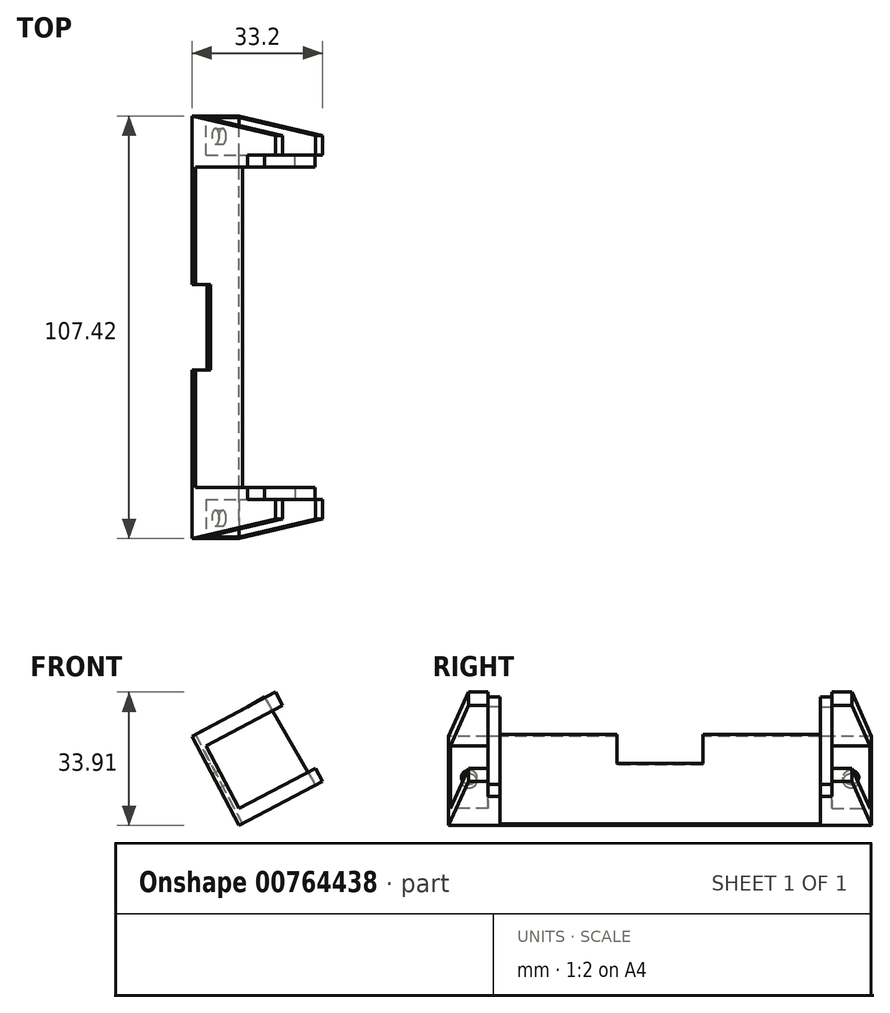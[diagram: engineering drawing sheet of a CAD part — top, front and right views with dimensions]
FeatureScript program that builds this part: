
annotation { "Feature Type Name" : "Feature", "Feature Type Description" : "" }
export const myFeature = defineFeature(function(context is Context, id is Id, definition is map)
    precondition{}
    {
        {
            var Q0;
            Q0=qCreatedBy(makeId("Right.planeOp"),FACE);
            var sketch = newSketch(context, id + "F0", { "sketchPlane" : qUnion([Q0])});
            skLineSegment(sketch, "E0.left", {"start": v(-41.6, -6.42) * mm, "end": v(-41.6, 6.2) * mm});
            skPoint(sketch, "E1.visualSharp", {"position": v(-41.6, 10.2) * mm});
            skPoint(sketch, "E2.visualSharp", {"position": v(-41.6, -10.42) * mm});
            skPoint(sketch, "E3.visualSharp", {"position": v(41.56, 10.2) * mm});
            skPoint(sketch, "E4.visualSharp", {"position": v(41.56, -10.42) * mm});
            skPoint(sketch, "E5.visualSharp", {"position": v(-38.3, -8.6) * mm});
            skPoint(sketch, "E6.visualSharp", {"position": v(38.25, -8.6) * mm});
            skLineSegment(sketch, "E7.bottom", {"start": v(-37.14, 9.3) * mm, "end": v(37.1, 9.3) * mm});
            skLineSegment(sketch, "E7.top", {"start": v(-37.14, -9.52) * mm, "end": v(37.1, -9.52) * mm});
            skLineSegment(sketch, "E7.left", {"start": v(-40.14, 6.3) * mm, "end": v(-40.14, -6.52) * mm});
            skLineSegment(sketch, "E7.right", {"start": v(40.1, 6.3) * mm, "end": v(40.1, -6.52) * mm});
            skArc(sketch, "E8.filletArc", {"start": v(-37.14, 9.3) * mm, "mid": v(-39.26, 8.42) * mm, "end": v(-40.14, 6.3) * mm});
            skPoint(sketch, "E9.visualSharp", {"position": v(-40.14, -9.52) * mm});
            skArc(sketch, "E9.filletArc", {"start": v(-40.14, -6.52) * mm, "mid": v(-39.26, -8.64) * mm, "end": v(-37.14, -9.52) * mm});
            skArc(sketch, "E10.filletArc", {"start": v(37.1, -9.52) * mm, "mid": v(39.21, -8.64) * mm, "end": v(40.1, -6.52) * mm});
            skArc(sketch, "E11.filletArc", {"start": v(40.1, 6.3) * mm, "mid": v(39.21, 8.42) * mm, "end": v(37.1, 9.3) * mm});
            skLineSegment(sketch, "E12.bottom", {"start": v(-43.7, 11.11) * mm, "end": v(43.7, 11.11) * mm});
            skLineSegment(sketch, "E12.top", {"start": v(-43.7, -11.11) * mm, "end": v(43.7, -11.11) * mm});
            skLineSegment(sketch, "E12.left", {"start": v(-43.7, 11.11) * mm, "end": v(-43.7, -11.11) * mm});
            skLineSegment(sketch, "E12.right", {"start": v(43.7, 11.11) * mm, "end": v(43.7, -11.11) * mm});
            skPoint(sketch, "E12.middle", {"position": v(0, 0) * mm});
            skLineSegment(sketch, "E13.bottom", {"start": v(-43.7, 11.11) * mm, "end": v(-41.6, 11.11) * mm});
            skLineSegment(sketch, "E13.top", {"start": v(-43.7, -11.11) * mm, "end": v(-41.6, -11.11) * mm});
            skLineSegment(sketch, "E13.right", {"start": v(-41.6, 11.11) * mm, "end": v(-41.6, -11.11) * mm});
            skLineSegment(sketch, "E14.bottom", {"start": v(43.7, 11.11) * mm, "end": v(41.56, 11.11) * mm});
            skLineSegment(sketch, "E14.top", {"start": v(43.7, -11.11) * mm, "end": v(41.56, -11.11) * mm});
            skLineSegment(sketch, "E14.right", {"start": v(41.56, 11.11) * mm, "end": v(41.56, -11.11) * mm});
            skSolve(sketch);
        }
        {
            var Q0;
            Q0=qSketchRegion(id+"F0",true);
            extrude(context, id + "F1", {"entities" : qUnion([Q0]), "depth" : 3 * mm, "offsetDistance" : 25 * mm});
        }
        {
            var Q0;
            Q0=makeQuery(id+"F1.opExtrude","SWEPT_FACE",FACE,{"disambiguationData":[OSD([sQuery(id+"F0.wireOp",EDGE,"E12.left")])]});
            var sketch = newSketch(context, id + "F2", { "sketchPlane" : qUnion([Q0])});
            skLineSegment(sketch, "E15", {"start": v(0, 11.11) * mm, "end": v(-12.83, 11.11) * mm});
            skLineSegment(sketch, "E16", {"start": v(-12.83, 11.11) * mm, "end": v(0, -11.11) * mm});
            skSolve(sketch);
        }
        {
            var Q0;
            Q0=qSketchRegion(id+"F2",true);
            var Q1;
            Q1=makeQuery(id+"F2.imprint","IMPRINT",FACE,{"disambiguationData":[TD([[makeQuery(id+"F2.imprint","IMPRINT",EDGE,{"derivedFrom":sQuery(id+"F2.wireOp",EDGE,"E15")}),1.0]])]});
            extrude(context, id + "F3", {"entities" : qUnion([Q0, Q1]), "operationType" : NewBodyOperationType.ADD, "oppositeDirection" : true, "depth" : 3 * mm, "offsetDistance" : 25 * mm});
        }
        {
            var Q0;
            Q0=makeQuery(id+"F1.opExtrude","SWEPT_FACE",FACE,{"disambiguationData":[OSD([sQuery(id+"F0.wireOp",EDGE,"E12.right")])]});
            var sketch = newSketch(context, id + "F4", { "sketchPlane" : qUnion([Q0])});
            skLineSegment(sketch, "E17", {"start": v(0, 11.11) * mm, "end": v(0, -11.11) * mm});
            skLineSegment(sketch, "E18", {"start": v(0, -11.11) * mm, "end": v(12.82, 11.12) * mm});
            skLineSegment(sketch, "E19", {"start": v(12.82, 11.12) * mm, "end": v(0, 11.11) * mm});
            skSolve(sketch);
        }
        {
            var Q0;
            Q0=makeQuery(id+"F4.imprint","IMPRINT",FACE,{"disambiguationData":[TD([[makeQuery(id+"F4.imprint","IMPRINT",EDGE,{"derivedFrom":sQuery(id+"F4.wireOp",EDGE,"E17")}),1.0]])]});
            extrude(context, id + "F5", {"entities" : qUnion([Q0]), "operationType" : NewBodyOperationType.ADD, "oppositeDirection" : true, "depth" : 3 * mm, "offsetDistance" : 25 * mm});
        }
        {
            var Q0;
            Q0=makeQuery(id+"F3.opExtrude","SWEPT_FACE",FACE,{"disambiguationData":[OSD([sQuery(id+"F2.wireOp",EDGE,"E16")])]});
            extrude(context, id + "F6", {"entities" : qUnion([Q0]), "operationType" : NewBodyOperationType.ADD, "depth" : 5 * mm, "offsetDistance" : 25 * mm});
        }
        {
            var Q0;
            {var subQ0=sQuery(id+"F2.wireOp",EDGE,"E16");var subQ1=sQuery(id+"F0.wireOp",EDGE,"E12.left");Q0=makeQuery(id+"F6.boolean.opBoolean","MERGE",FACE,{"derivedFrom":[makeQuery(id+"F3.boolean.opBoolean","MERGE",FACE,{"derivedFrom":[makeQuery(id+"F1.opExtrude","SWEPT_FACE",FACE,{"disambiguationData":[OSD([subQ1])]}),makeQuery(id+"F3.opExtrude","CAP_FACE",FACE,{"disambiguationData":[OSD([subQ1,sQuery(id+"F2.wireOp",EDGE,"E15"),subQ0])],"isStart":true})]}),makeQuery(id+"F6.opExtrude","SWEPT_FACE",FACE,{"disambiguationData":[OSD([subQ0]),TDD([makeQuery(id+"F3.opExtrude","CAP_EDGE",EDGE,{"disambiguationData":[OSD([subQ0])],"isStart":true})])]})]});}
            var sketch = newSketch(context, id + "F7", { "sketchPlane" : qUnion([Q0])});
            skLineSegment(sketch, "E20", {"start": v(-2.17, -12.36) * mm, "end": v(-5.2, -14.11) * mm});
            skLineSegment(sketch, "E21", {"start": v(-5.2, -14.11) * mm, "end": v(-17.16, 8.61) * mm});
            skSolve(sketch);
        }
        {
            var Q0;
            {var subQ3=sQuery(id+"F7.wireOp",EDGE,"E21");Q0=makeQuery(id+"F7.imprint","IMPRINT",FACE,{"disambiguationData":[TD([[makeQuery(id+"F7.imprint","IMPRINT",EDGE,{"derivedFrom":subQ3}),-1.0]])]});}
            extrude(context, id + "F8", {"entities" : qUnion([Q0]), "operationType" : NewBodyOperationType.ADD, "oppositeDirection" : true, "depth" : 3 * mm, "offsetDistance" : 25 * mm});
        }
        {
            var Q0;
            Q0=makeQuery(id+"F5.opExtrude","SWEPT_FACE",FACE,{"disambiguationData":[OSD([sQuery(id+"F4.wireOp",EDGE,"E18")])]});
            extrude(context, id + "F9", {"entities" : qUnion([Q0]), "operationType" : NewBodyOperationType.ADD, "depth" : 5 * mm, "offsetDistance" : 25 * mm});
        }
        {
            var Q0;
            {var subQ0=sQuery(id+"F4.wireOp",EDGE,"E18");Q0=makeQuery(id+"F9.boolean.opBoolean","MERGE",FACE,{"derivedFrom":[makeQuery(id+"F5.boolean.opBoolean","MERGE",FACE,{"derivedFrom":[makeQuery(id+"F1.opExtrude","SWEPT_FACE",FACE,{"disambiguationData":[OSD([sQuery(id+"F0.wireOp",EDGE,"E12.right")])]}),makeQuery(id+"F5.opExtrude","CAP_FACE",FACE,{"disambiguationData":[OSD([sQuery(id+"F4.wireOp",EDGE,"E17"),subQ0,sQuery(id+"F4.wireOp",EDGE,"E19")])],"isStart":true})]}),makeQuery(id+"F9.opExtrude","SWEPT_FACE",FACE,{"disambiguationData":[OSD([subQ0]),TDD([makeQuery(id+"F5.opExtrude","CAP_EDGE",EDGE,{"disambiguationData":[OSD([subQ0])],"isStart":true})])]})]});}
            var sketch = newSketch(context, id + "F10", { "sketchPlane" : qUnion([Q0])});
            skLineSegment(sketch, "E22", {"start": v(4.33, -13.61) * mm, "end": v(5.2, -14.11) * mm});
            skLineSegment(sketch, "E23", {"start": v(5.2, -14.11) * mm, "end": v(17.16, 8.62) * mm});
            skSolve(sketch);
        }
        {
            var Q0;
            Q0=makeQuery(id+"F10.imprint","IMPRINT",FACE,{"disambiguationData":[TD([[makeQuery(id+"F10.imprint","IMPRINT",EDGE,{"derivedFrom":sQuery(id+"F10.wireOp",EDGE,"E22")}),1.0]])]});
            extrude(context, id + "F11", {"entities" : qUnion([Q0]), "operationType" : NewBodyOperationType.ADD, "oppositeDirection" : true, "depth" : 3 * mm, "offsetDistance" : 25 * mm});
        }
        {
            var Q0;
            Q0=makeQuery(id+"F11.opExtrude","SWEPT_FACE",FACE,{"disambiguationData":[OSD([sQuery(id+"F10.wireOp",EDGE,"E23")])]});
            extrude(context, id + "F12", {"entities" : qUnion([Q0]), "operationType" : NewBodyOperationType.ADD, "depth" : 16 * mm, "offsetDistance" : 25 * mm});
        }
        {
            var Q0;
            Q0=makeQuery(id+"F8.opExtrude","SWEPT_FACE",FACE,{"disambiguationData":[OSD([sQuery(id+"F7.wireOp",EDGE,"E21")])]});
            extrude(context, id + "F13", {"entities" : qUnion([Q0]), "operationType" : NewBodyOperationType.ADD, "depth" : 16 * mm, "offsetDistance" : 25 * mm});
        }
        {
            var Q0;
            Q0=makeQuery(id+"F13.opExtrude","SWEPT_FACE",FACE,{"disambiguationData":[OSD([sQuery(id+"F7.wireOp",EDGE,"E20"),sQuery(id+"F7.wireOp",EDGE,"E21")])]});
            var sketch = newSketch(context, id + "F14", { "sketchPlane" : qUnion([Q0])});
            skLineSegment(sketch, "E24", {"start": v(-27.17, 43.7) * mm, "end": v(-27.17, -43.7) * mm});
            skLineSegment(sketch, "E25", {"start": v(-27.17, -43.7) * mm, "end": v(-26.17, -43.7) * mm});
            skLineSegment(sketch, "E26", {"start": v(-26.17, -43.7) * mm, "end": v(-26.17, 43.7) * mm});
            skLineSegment(sketch, "E27", {"start": v(-26.17, 43.7) * mm, "end": v(-27.17, 43.7) * mm});
            skSolve(sketch);
        }
        {
            var Q0;
            {var subQ0=sQuery(id+"F14.wireOp",EDGE,"E27");Q0=makeQuery(id+"F14.imprint","IMPRINT",FACE,{"disambiguationData":[TD([[makeQuery(id+"F14.imprint","IMPRINT",EDGE,{"derivedFrom":subQ0}),-1.0]])]});}
            var Q1;
            {var subQ5=sQuery(id+"F14.wireOp",EDGE,"E25");Q1=makeQuery(id+"F14.imprint","IMPRINT",FACE,{"disambiguationData":[TD([[makeQuery(id+"F14.imprint","IMPRINT",EDGE,{"derivedFrom":subQ5}),1.0]])]});}
            extrude(context, id + "F15", {"entities" : qUnion([Q0, Q1]), "oppositeDirection" : true, "depth" : 25.68 * mm, "offsetDistance" : 25 * mm});
        }
        {
            var Q0;
            Q0=makeQuery(id+"F15.opExtrude","SWEPT_FACE",FACE,{"disambiguationData":[OSD([sQuery(id+"F14.wireOp",EDGE,"E25")])]});
            extrude(context, id + "F16", {"entities" : qUnion([Q0]), "depth" : 10 * mm, "offsetDistance" : 25 * mm});
        }
        {
            var Q0;
            Q0=makeQuery(id+"F16.opExtrude","SWEPT_FACE",FACE,{"disambiguationData":[OSD([sQuery(id+"F14.wireOp",EDGE,"E25"),sQuery(id+"F14.wireOp",EDGE,"E26")])]});
            extrude(context, id + "F17", {"entities" : qUnion([Q0]), "depth" : 2 * mm, "offsetDistance" : 25 * mm});
        }
        {
            var Q0;
            Q0=makeQuery(id+"F15.opExtrude","SWEPT_FACE",FACE,{"disambiguationData":[OSD([sQuery(id+"F14.wireOp",EDGE,"E27")])]});
            extrude(context, id + "F18", {"entities" : qUnion([Q0]), "depth" : 10 * mm, "offsetDistance" : 25 * mm});
        }
        {
            var Q0;
            Q0=makeQuery(id+"F18.opExtrude","SWEPT_FACE",FACE,{"disambiguationData":[OSD([sQuery(id+"F7.wireOp",EDGE,"E20"),sQuery(id+"F7.wireOp",EDGE,"E21"),sQuery(id+"F14.wireOp",EDGE,"E26"),sQuery(id+"F14.wireOp",EDGE,"E27")])]});
            extrude(context, id + "F19", {"entities" : qUnion([Q0]), "depth" : 2 * mm, "offsetDistance" : 25 * mm});
        }
        {
            var Q0;
            Q0=makeQuery(id+"F15.opExtrude","SWEPT_BODY",BODY,{"disambiguationData":[OSD([sQuery(id+"F14.wireOp",EDGE,"E24"),sQuery(id+"F14.wireOp",EDGE,"E25"),sQuery(id+"F14.wireOp",EDGE,"E26"),sQuery(id+"F14.wireOp",EDGE,"E27")])]});
            var Q1;
            Q1=makeQuery(id+"F17.opExtrude","SWEPT_BODY",BODY,{"disambiguationData":[OSD([sQuery(id+"F14.wireOp",EDGE,"E25"),sQuery(id+"F14.wireOp",EDGE,"E26")])]});
            var Q2;
            Q2=makeQuery(id+"F16.opExtrude","SWEPT_BODY",BODY,{"disambiguationData":[OSD([sQuery(id+"F14.wireOp",EDGE,"E25")])]});
            var Q3;
            Q3=makeQuery(id+"F19.opExtrude","SWEPT_BODY",BODY,{"disambiguationData":[OSD([sQuery(id+"F7.wireOp",EDGE,"E20"),sQuery(id+"F7.wireOp",EDGE,"E21"),sQuery(id+"F14.wireOp",EDGE,"E26"),sQuery(id+"F14.wireOp",EDGE,"E27")])]});
            var Q4;
            Q4=makeQuery(id+"F18.opExtrude","SWEPT_BODY",BODY,{"disambiguationData":[OSD([sQuery(id+"F14.wireOp",EDGE,"E27")])]});
            booleanBodies(context, id + "F20", {"operationType" : BooleanOperationType.UNION, "tools" : qUnion([Q0, Q1, Q2, Q3, Q4])});
        }
        {
            var Q0;
            Q0=makeQuery(id+"F15.opExtrude","SWEPT_BODY",BODY,{"disambiguationData":[OSD([sQuery(id+"F14.wireOp",EDGE,"E24"),sQuery(id+"F14.wireOp",EDGE,"E25"),sQuery(id+"F14.wireOp",EDGE,"E26"),sQuery(id+"F14.wireOp",EDGE,"E27")])]});
            var Q1;
            Q1=makeQuery(id+"F1.opExtrude","SWEPT_BODY",BODY,{"disambiguationData":[OSD([sQuery(id+"F0.wireOp",EDGE,"E7.bottom"),sQuery(id+"F0.wireOp",EDGE,"E7.top"),sQuery(id+"F0.wireOp",EDGE,"E7.left"),sQuery(id+"F0.wireOp",EDGE,"E7.right"),sQuery(id+"F0.wireOp",EDGE,"E8.filletArc"),sQuery(id+"F0.wireOp",EDGE,"E9.filletArc"),sQuery(id+"F0.wireOp",EDGE,"E10.filletArc"),sQuery(id+"F0.wireOp",EDGE,"E11.filletArc"),sQuery(id+"F0.wireOp",EDGE,"E12.bottom"),sQuery(id+"F0.wireOp",EDGE,"E12.top"),sQuery(id+"F0.wireOp",EDGE,"E13.bottom"),sQuery(id+"F0.wireOp",EDGE,"E13.top"),sQuery(id+"F0.wireOp",EDGE,"E12.left"),sQuery(id+"F0.wireOp",EDGE,"E14.bottom"),sQuery(id+"F0.wireOp",EDGE,"E14.top"),sQuery(id+"F0.wireOp",EDGE,"E12.right")])]});
            booleanBodies(context, id + "F21", {"operationType" : BooleanOperationType.UNION, "tools" : qUnion([Q0, Q1])});
        }
        {
            var Q0;
            Q0=makeQuery(id+"F19.opExtrude","CAP_FACE",FACE,{"disambiguationData":[OSD([sQuery(id+"F7.wireOp",EDGE,"E20"),sQuery(id+"F7.wireOp",EDGE,"E21"),sQuery(id+"F14.wireOp",EDGE,"E26"),sQuery(id+"F14.wireOp",EDGE,"E27")])],"isStart":false});
            extrude(context, id + "F22", {"entities" : qUnion([Q0]), "operationType" : NewBodyOperationType.ADD, "depth" : 21 * mm, "offsetDistance" : 25 * mm});
        }
        {
            var Q0;
            {var subQ0=sQuery(id+"F14.wireOp",EDGE,"E27");var subQ1=sQuery(id+"F14.wireOp",EDGE,"E26");var subQ2=sQuery(id+"F7.wireOp",EDGE,"E21");var subQ3=sQuery(id+"F7.wireOp",EDGE,"E20");var subQ4=makeQuery(id+"F18.opExtrude","SWEPT_EDGE",EDGE,{"disambiguationData":[OSD([subQ3,subQ2,subQ1,subQ0]),TDD([makeQuery(id+"F15.opExtrude","CAP_VERTEX",VERTEX,{"disambiguationData":[OSD([subQ3,subQ2,subQ1,subQ0])],"isStart":true})])]});var subQ5=sQuery(id+"F14.wireOp",EDGE,"E25");Q0=makeQuery(id+"F22.boolean.opBoolean","MERGE",FACE,{"derivedFrom":[makeQuery(id+"F21.opBoolean","MERGE",FACE,{"derivedFrom":[makeQuery(id+"F13.opExtrude","SWEPT_FACE",FACE,{"disambiguationData":[OSD([subQ3,subQ2])]}),makeQuery(id+"F20.opBoolean","MERGE",FACE,{"derivedFrom":[makeQuery(id+"F15.opExtrude","CAP_FACE",FACE,{"disambiguationData":[OSD([sQuery(id+"F14.wireOp",EDGE,"E24"),subQ5,subQ1,subQ0])],"isStart":true}),makeQuery(id+"F16.opExtrude","SWEPT_FACE",FACE,{"disambiguationData":[OSD([subQ5]),TDD([makeQuery(id+"F15.opExtrude","CAP_EDGE",EDGE,{"disambiguationData":[OSD([subQ5])],"isStart":true})])]}),makeQuery(id+"F17.opExtrude","SWEPT_FACE",FACE,{"disambiguationData":[OSD([subQ5,subQ1]),TDD([makeQuery(id+"F16.opExtrude","SWEPT_EDGE",EDGE,{"disambiguationData":[OSD([subQ5,subQ1]),TDD([makeQuery(id+"F15.opExtrude","CAP_VERTEX",VERTEX,{"disambiguationData":[OSD([subQ5,subQ1])],"isStart":true})])]})])]}),makeQuery(id+"F18.opExtrude","SWEPT_FACE",FACE,{"disambiguationData":[OSD([subQ0]),TDD([makeQuery(id+"F15.opExtrude","CAP_EDGE",EDGE,{"disambiguationData":[OSD([subQ0])],"isStart":true})])]}),makeQuery(id+"F19.opExtrude","SWEPT_FACE",FACE,{"disambiguationData":[OSD([subQ3,subQ2,subQ1,subQ0]),TDD([subQ4])]})]})]}),makeQuery(id+"F22.opExtrude","SWEPT_FACE",FACE,{"disambiguationData":[OSD([subQ3,subQ2,subQ1,subQ0]),TDD([makeQuery(id+"F19.opExtrude","CAP_EDGE",EDGE,{"disambiguationData":[OSD([subQ3,subQ2,subQ1,subQ0]),TDD([subQ4])],"isStart":false})])]})]});}
            var sketch = newSketch(context, id + "F23", { "sketchPlane" : qUnion([Q0])});
            skLineSegment(sketch, "E28", {"start": v(-27.17, 53.7) * mm, "end": v(-3.17, 48.7) * mm});
            skLineSegment(sketch, "E29", {"start": v(-3.17, 48.7) * mm, "end": v(-3.17, 53.7) * mm});
            skLineSegment(sketch, "E30", {"start": v(-3.17, 53.7) * mm, "end": v(-27.17, 53.7) * mm});
            skSolve(sketch);
        }
        {
            var Q0;
            Q0=makeQuery(id+"F23.imprint","IMPRINT",FACE,{"disambiguationData":[TD([[makeQuery(id+"F23.imprint","IMPRINT",EDGE,{"derivedFrom":sQuery(id+"F23.wireOp",EDGE,"E28")}),1.0]])]});
            extrude(context, id + "F24", {"entities" : qUnion([Q0]), "operationType" : NewBodyOperationType.REMOVE, "oppositeDirection" : true, "depth" : 26 * mm, "offsetDistance" : 25 * mm});
        }
        {
            var Q0;
            Q0=makeQuery(id+"F22.opExtrude","CAP_FACE",FACE,{"disambiguationData":[OSD([sQuery(id+"F7.wireOp",EDGE,"E20"),sQuery(id+"F7.wireOp",EDGE,"E21"),sQuery(id+"F14.wireOp",EDGE,"E26"),sQuery(id+"F14.wireOp",EDGE,"E27")])],"isStart":false});
            var sketch = newSketch(context, id + "F25", { "sketchPlane" : qUnion([Q0])});
            skLineSegment(sketch, "E31.bottom", {"start": v(-43.7, 11.78) * mm, "end": v(-53.7, 11.78) * mm});
            skLineSegment(sketch, "E31.top", {"start": v(-43.7, -6.22) * mm, "end": v(-53.7, -6.22) * mm});
            skLineSegment(sketch, "E31.left", {"start": v(-43.7, 11.78) * mm, "end": v(-43.7, -6.22) * mm});
            skLineSegment(sketch, "E31.right", {"start": v(-53.7, 11.78) * mm, "end": v(-53.7, -6.22) * mm});
            skPoint(sketch, "E31.middle", {"position": v(-48.7, 2.78) * mm});
            skSolve(sketch);
        }
        {
            var Q0;
            {var subQ0=sQuery(id+"F25.wireOp",EDGE,"E31.left");Q0=makeQuery(id+"F25.imprint","IMPRINT",FACE,{"disambiguationData":[TD([[makeQuery(id+"F25.imprint","IMPRINT",EDGE,{"derivedFrom":subQ0}),-1.0]])]});}
            var Q1;
            {var subQ0=sQuery(id+"F25.wireOp",EDGE,"E31.right");Q1=makeQuery(id+"F25.imprint","IMPRINT",FACE,{"disambiguationData":[TD([[makeQuery(id+"F25.imprint","IMPRINT",EDGE,{"derivedFrom":subQ0}),1.0]])]});}
            extrude(context, id + "F26", {"entities" : qUnion([Q0, Q1]), "operationType" : NewBodyOperationType.REMOVE, "oppositeDirection" : true, "depth" : 22 * mm, "offsetDistance" : 25 * mm});
        }
        {
            var Q0;
            Q0=makeQuery(id+"F17.opExtrude","CAP_FACE",FACE,{"disambiguationData":[OSD([sQuery(id+"F14.wireOp",EDGE,"E25"),sQuery(id+"F14.wireOp",EDGE,"E26")])],"isStart":false});
            extrude(context, id + "F27", {"entities" : qUnion([Q0]), "operationType" : NewBodyOperationType.ADD, "depth" : 21 * mm, "offsetDistance" : 25 * mm});
        }
        {
            var Q0;
            {var subQ0=sQuery(id+"F14.wireOp",EDGE,"E26");var subQ1=sQuery(id+"F14.wireOp",EDGE,"E25");var subQ2=makeQuery(id+"F16.opExtrude","SWEPT_EDGE",EDGE,{"disambiguationData":[OSD([subQ1,subQ0]),TDD([makeQuery(id+"F15.opExtrude","CAP_VERTEX",VERTEX,{"disambiguationData":[OSD([subQ1,subQ0])],"isStart":true})])]});var subQ3=sQuery(id+"F14.wireOp",EDGE,"E27");var subQ4=sQuery(id+"F7.wireOp",EDGE,"E21");var subQ5=sQuery(id+"F7.wireOp",EDGE,"E20");var subQ6=makeQuery(id+"F18.opExtrude","SWEPT_EDGE",EDGE,{"disambiguationData":[OSD([subQ5,subQ4,subQ0,subQ3]),TDD([makeQuery(id+"F15.opExtrude","CAP_VERTEX",VERTEX,{"disambiguationData":[OSD([subQ5,subQ4,subQ0,subQ3])],"isStart":true})])]});Q0=makeQuery(id+"F27.boolean.opBoolean","MERGE",FACE,{"derivedFrom":[makeQuery(id+"F22.boolean.opBoolean","MERGE",FACE,{"derivedFrom":[makeQuery(id+"F21.opBoolean","MERGE",FACE,{"derivedFrom":[makeQuery(id+"F13.opExtrude","SWEPT_FACE",FACE,{"disambiguationData":[OSD([subQ5,subQ4])]}),makeQuery(id+"F20.opBoolean","MERGE",FACE,{"derivedFrom":[makeQuery(id+"F15.opExtrude","CAP_FACE",FACE,{"disambiguationData":[OSD([sQuery(id+"F14.wireOp",EDGE,"E24"),subQ1,subQ0,subQ3])],"isStart":true}),makeQuery(id+"F16.opExtrude","SWEPT_FACE",FACE,{"disambiguationData":[OSD([subQ1]),TDD([makeQuery(id+"F15.opExtrude","CAP_EDGE",EDGE,{"disambiguationData":[OSD([subQ1])],"isStart":true})])]}),makeQuery(id+"F17.opExtrude","SWEPT_FACE",FACE,{"disambiguationData":[OSD([subQ1,subQ0]),TDD([subQ2])]}),makeQuery(id+"F18.opExtrude","SWEPT_FACE",FACE,{"disambiguationData":[OSD([subQ3]),TDD([makeQuery(id+"F15.opExtrude","CAP_EDGE",EDGE,{"disambiguationData":[OSD([subQ3])],"isStart":true})])]}),makeQuery(id+"F19.opExtrude","SWEPT_FACE",FACE,{"disambiguationData":[OSD([subQ5,subQ4,subQ0,subQ3]),TDD([subQ6])]})]})]}),makeQuery(id+"F22.opExtrude","SWEPT_FACE",FACE,{"disambiguationData":[OSD([subQ5,subQ4,subQ0,subQ3]),TDD([makeQuery(id+"F19.opExtrude","CAP_EDGE",EDGE,{"disambiguationData":[OSD([subQ5,subQ4,subQ0,subQ3]),TDD([subQ6])],"isStart":false})])]})]}),makeQuery(id+"F27.opExtrude","SWEPT_FACE",FACE,{"disambiguationData":[OSD([subQ1,subQ0]),TDD([makeQuery(id+"F17.opExtrude","CAP_EDGE",EDGE,{"disambiguationData":[OSD([subQ1,subQ0]),TDD([subQ2])],"isStart":false})])]})]});}
            var sketch = newSketch(context, id + "F28", { "sketchPlane" : qUnion([Q0])});
            skLineSegment(sketch, "E32", {"start": v(-3.17, -48.7) * mm, "end": v(-27.17, -53.7) * mm});
            skLineSegment(sketch, "E33", {"start": v(-27.17, -53.7) * mm, "end": v(-3.17, -53.7) * mm});
            skLineSegment(sketch, "E34", {"start": v(-3.17, -53.7) * mm, "end": v(-3.17, -48.7) * mm});
            skSolve(sketch);
        }
        {
            var Q0;
            Q0=makeQuery(id+"F28.imprint","IMPRINT",FACE,{"disambiguationData":[TD([[makeQuery(id+"F28.imprint","IMPRINT",EDGE,{"derivedFrom":sQuery(id+"F28.wireOp",EDGE,"E32")}),1.0]])]});
            extrude(context, id + "F29", {"entities" : qUnion([Q0]), "operationType" : NewBodyOperationType.REMOVE, "oppositeDirection" : true, "depth" : 29.1 * mm, "offsetDistance" : 25 * mm});
        }
        {
            var Q0;
            Q0=makeQuery(id+"F27.opExtrude","CAP_FACE",FACE,{"disambiguationData":[OSD([sQuery(id+"F14.wireOp",EDGE,"E25"),sQuery(id+"F14.wireOp",EDGE,"E26")])],"isStart":false});
            var sketch = newSketch(context, id + "F30", { "sketchPlane" : qUnion([Q0])});
            skLineSegment(sketch, "E35.bottom", {"start": v(43.7, -6.22) * mm, "end": v(53.7, -6.22) * mm});
            skLineSegment(sketch, "E35.top", {"start": v(43.7, 11.78) * mm, "end": v(53.7, 11.78) * mm});
            skLineSegment(sketch, "E35.left", {"start": v(43.7, -6.22) * mm, "end": v(43.7, 11.78) * mm});
            skLineSegment(sketch, "E35.right", {"start": v(53.7, -6.22) * mm, "end": v(53.7, 11.78) * mm});
            skPoint(sketch, "E35.middle", {"position": v(48.7, 2.78) * mm});
            skSolve(sketch);
        }
        {
            var Q0;
            {var subQ0=sQuery(id+"F30.wireOp",EDGE,"E35.left");Q0=makeQuery(id+"F30.imprint","IMPRINT",FACE,{"disambiguationData":[TD([[makeQuery(id+"F30.imprint","IMPRINT",EDGE,{"derivedFrom":subQ0}),1.0]])]});}
            var Q1;
            {var subQ0=sQuery(id+"F30.wireOp",EDGE,"E35.right");Q1=makeQuery(id+"F30.imprint","IMPRINT",FACE,{"disambiguationData":[TD([[makeQuery(id+"F30.imprint","IMPRINT",EDGE,{"derivedFrom":subQ0}),1.0]])]});}
            extrude(context, id + "F31", {"entities" : qUnion([Q0, Q1]), "operationType" : NewBodyOperationType.REMOVE, "oppositeDirection" : true, "depth" : 22 * mm, "offsetDistance" : 25 * mm});
        }
        {
            var Q0;
            Q0=makeQuery(id+"F31.boolean.opBoolean","COPY",FACE,{"derivedFrom":makeQuery(id+"F31.opExtrude","CAP_FACE",FACE,{"disambiguationData":[OSD([sQuery(id+"F30.wireOp",EDGE,"E35.bottom"),sQuery(id+"F30.wireOp",EDGE,"E35.top"),sQuery(id+"F30.wireOp",EDGE,"E35.left"),sQuery(id+"F30.wireOp",EDGE,"E35.right")])],"isStart":false})});
            var sketch = newSketch(context, id + "F32", { "sketchPlane" : qUnion([Q0])});
            skCircle(sketch, "E36", {"center": v(48.5, 2.78) * mm, "radius": 2 * mm});
            skPoint(sketch, "E36.centerSnap0", {"position": v(48.5, 11.78) * mm});
            skPoint(sketch, "E36.centerSnap1", {"position": v(53.29, 2.78) * mm});
            skSolve(sketch);
        }
        {
            var Q0;
            Q0 = qSketchRegion(id + "F32", true);
            extrude(context, id + "F33", {"entities" : qUnion([Q0]), "operationType" : NewBodyOperationType.REMOVE, "oppositeDirection" : true, "depth" : 25 * mm, "offsetDistance" : 25 * mm});
        }
        {
            var Q0;
            Q0=makeQuery(id+"F26.boolean.opBoolean","COPY",FACE,{"derivedFrom":makeQuery(id+"F26.opExtrude","CAP_FACE",FACE,{"disambiguationData":[OSD([sQuery(id+"F25.wireOp",EDGE,"E31.bottom"),sQuery(id+"F25.wireOp",EDGE,"E31.top"),sQuery(id+"F25.wireOp",EDGE,"E31.left"),sQuery(id+"F25.wireOp",EDGE,"E31.right")])],"isStart":false})});
            var sketch = newSketch(context, id + "F34", { "sketchPlane" : qUnion([Q0])});
            skCircle(sketch, "E37", {"center": v(-48.5, 2.78) * mm, "radius": 2 * mm});
            skPoint(sketch, "E37.centerSnap0", {"position": v(-53.29, 2.78) * mm});
            skPoint(sketch, "E37.centerSnap1", {"position": v(-48.5, -6.22) * mm});
            skSolve(sketch);
        }
        {
            var Q0;
            Q0 = qSketchRegion(id + "F34", true);
            extrude(context, id + "F35", {"entities" : qUnion([Q0]), "operationType" : NewBodyOperationType.REMOVE, "oppositeDirection" : true, "depth" : 25 * mm, "offsetDistance" : 25 * mm});
        }
        {
            var Q0;
            {var subQ0=sQuery(id+"F2.wireOp",EDGE,"E16");var subQ1=sQuery(id+"F0.wireOp",EDGE,"E12.left");Q0=makeQuery(id+"F8.boolean.opBoolean","MERGE",FACE,{"derivedFrom":[makeQuery(id+"F6.boolean.opBoolean","MERGE",FACE,{"derivedFrom":[makeQuery(id+"F3.boolean.opBoolean","MERGE",FACE,{"derivedFrom":[makeQuery(id+"F1.opExtrude","SWEPT_FACE",FACE,{"disambiguationData":[OSD([subQ1])]}),makeQuery(id+"F3.opExtrude","CAP_FACE",FACE,{"disambiguationData":[OSD([subQ1,sQuery(id+"F2.wireOp",EDGE,"E15"),subQ0])],"isStart":true})]}),makeQuery(id+"F6.opExtrude","SWEPT_FACE",FACE,{"disambiguationData":[OSD([subQ0]),TDD([makeQuery(id+"F3.opExtrude","CAP_EDGE",EDGE,{"disambiguationData":[OSD([subQ0])],"isStart":true})])]})]}),makeQuery(id+"F8.opExtrude","CAP_FACE",FACE,{"disambiguationData":[OSD([subQ0,sQuery(id+"F7.wireOp",EDGE,"E20"),sQuery(id+"F7.wireOp",EDGE,"E21")])],"isStart":true})]});}
            var sketch = newSketch(context, id + "F36", { "sketchPlane" : qUnion([Q0])});
            skLineSegment(sketch, "E38", {"start": v(-12.83, 11.11) * mm, "end": v(0, -11.11) * mm});
            skLineSegment(sketch, "E39", {"start": v(0, -11.11) * mm, "end": v(3, -11.11) * mm});
            skLineSegment(sketch, "E40", {"start": v(3, -11.11) * mm, "end": v(3, 11.11) * mm});
            skLineSegment(sketch, "E41", {"start": v(3, 11.11) * mm, "end": v(-12.83, 11.11) * mm});
            skSolve(sketch);
        }
        {
            var Q0;
            Q0 = qSketchRegion(id + "F36", true);
            extrude(context, id + "F37", {"entities" : qUnion([Q0]), "operationType" : NewBodyOperationType.REMOVE, "oppositeDirection" : true, "depth" : 87 * mm, "offsetDistance" : 25 * mm});
        }
        {
            var Q0;
            {var subQ0=sQuery(id+"F10.wireOp",EDGE,"E23");var subQ1=sQuery(id+"F4.wireOp",EDGE,"E18");Q0=makeQuery(id+"F12.boolean.opBoolean","MERGE",FACE,{"derivedFrom":[makeQuery(id+"F11.boolean.opBoolean","MERGE",FACE,{"derivedFrom":[makeQuery(id+"F9.boolean.opBoolean","MERGE",FACE,{"derivedFrom":[makeQuery(id+"F5.boolean.opBoolean","MERGE",FACE,{"derivedFrom":[makeQuery(id+"F1.opExtrude","SWEPT_FACE",FACE,{"disambiguationData":[OSD([sQuery(id+"F0.wireOp",EDGE,"E12.right")])]}),makeQuery(id+"F5.opExtrude","CAP_FACE",FACE,{"disambiguationData":[OSD([sQuery(id+"F4.wireOp",EDGE,"E17"),subQ1,sQuery(id+"F4.wireOp",EDGE,"E19")])],"isStart":true})]}),makeQuery(id+"F9.opExtrude","SWEPT_FACE",FACE,{"disambiguationData":[OSD([subQ1]),TDD([makeQuery(id+"F5.opExtrude","CAP_EDGE",EDGE,{"disambiguationData":[OSD([subQ1])],"isStart":true})])]})]}),makeQuery(id+"F11.opExtrude","CAP_FACE",FACE,{"disambiguationData":[OSD([subQ1,sQuery(id+"F10.wireOp",EDGE,"E22"),subQ0])],"isStart":true})]}),makeQuery(id+"F12.opExtrude","SWEPT_FACE",FACE,{"disambiguationData":[OSD([subQ0]),TDD([makeQuery(id+"F11.opExtrude","CAP_EDGE",EDGE,{"disambiguationData":[OSD([subQ0])],"isStart":true})])]})]});}
            var sketch = newSketch(context, id + "F38", { "sketchPlane" : qUnion([Q0])});
            skLineSegment(sketch, "E42", {"start": v(-3, 11.11) * mm, "end": v(-3, -11.11) * mm});
            skLineSegment(sketch, "E43", {"start": v(-3, -11.11) * mm, "end": v(0, -11.11) * mm});
            skLineSegment(sketch, "E44", {"start": v(0, -11.11) * mm, "end": v(12.82, 11.12) * mm});
            skLineSegment(sketch, "E45", {"start": v(12.82, 11.12) * mm, "end": v(-3, 11.11) * mm});
            skSolve(sketch);
        }
        {
            var Q0;
            Q0 = qSketchRegion(id + "F38", true);
            extrude(context, id + "F39", {"entities" : qUnion([Q0]), "operationType" : NewBodyOperationType.REMOVE, "oppositeDirection" : true, "depth" : 25 * mm, "offsetDistance" : 25 * mm});
        }
        {
            var Q0;
            {var subQ0=sQuery(id+"F14.wireOp",EDGE,"E24");Q0=makeQuery(id+"F20.opBoolean","MERGE",FACE,{"derivedFrom":[makeQuery(id+"F15.opExtrude","SWEPT_FACE",FACE,{"disambiguationData":[OSD([subQ0])]}),makeQuery(id+"F16.opExtrude","SWEPT_FACE",FACE,{"disambiguationData":[OSD([subQ0,sQuery(id+"F14.wireOp",EDGE,"E25")])]}),makeQuery(id+"F18.opExtrude","SWEPT_FACE",FACE,{"disambiguationData":[OSD([subQ0,sQuery(id+"F14.wireOp",EDGE,"E27")])]})]});}
            var sketch = newSketch(context, id + "F40", { "sketchPlane" : qUnion([Q0])});
            skLineSegment(sketch, "E46.bottom", {"start": v(-10.9, 7.34) * mm, "end": v(10.9, 7.34) * mm});
            skLineSegment(sketch, "E46.top", {"start": v(-10.9, 27.54) * mm, "end": v(10.9, 27.54) * mm});
            skLineSegment(sketch, "E46.left", {"start": v(-10.9, 7.34) * mm, "end": v(-10.9, 27.54) * mm});
            skLineSegment(sketch, "E46.right", {"start": v(10.9, 7.34) * mm, "end": v(10.9, 27.54) * mm});
            skPoint(sketch, "E46.middle", {"position": v(0, 17.44) * mm});
            skSolve(sketch);
        }
        {
            var Q0;
            {var subQ0=sQuery(id+"F40.wireOp",EDGE,"E46.bottom");Q0=makeQuery(id+"F40.imprint","IMPRINT",FACE,{"disambiguationData":[TD([[makeQuery(id+"F40.imprint","IMPRINT",EDGE,{"derivedFrom":subQ0}),1.0]])]});}
            extrude(context, id + "F41", {"entities" : qUnion([Q0]), "operationType" : NewBodyOperationType.REMOVE, "oppositeDirection" : true, "depth" : 25 * mm, "offsetDistance" : 25 * mm});
        }
    });
